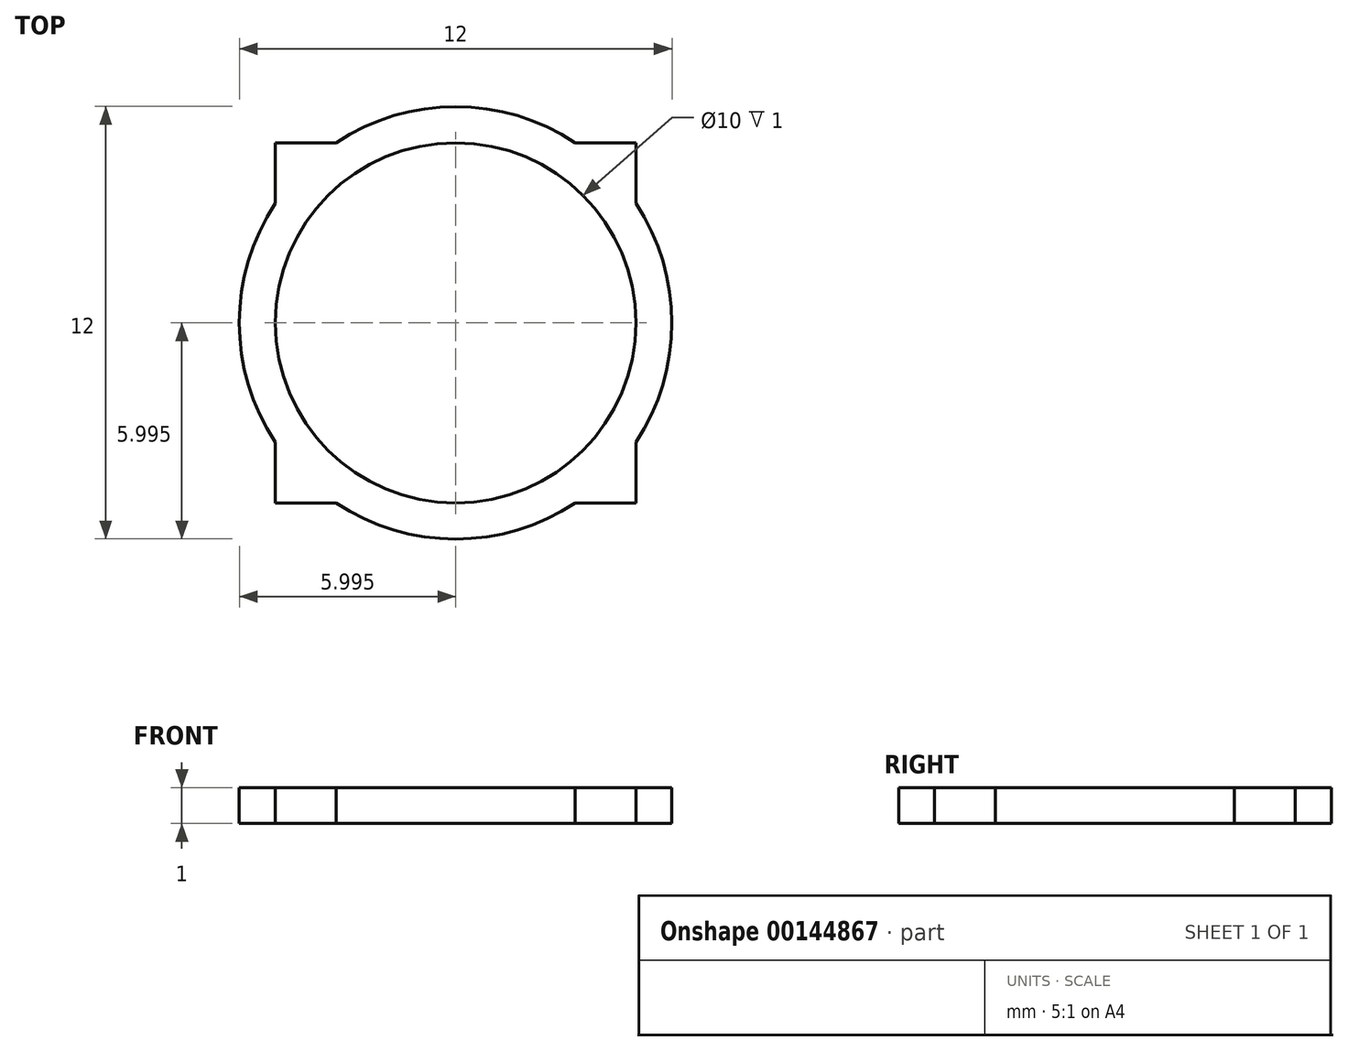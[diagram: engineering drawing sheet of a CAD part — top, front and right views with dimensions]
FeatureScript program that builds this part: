
annotation { "Feature Type Name" : "Feature", "Feature Type Description" : "" }
export const myFeature = defineFeature(function(context is Context, id is Id, definition is map)
    precondition{}
    {
        {
            var Q0;
            Q0=qCreatedBy(makeId("Top.planeOp"),FACE);
            var sketch = newSketch(context, id + "F0", { "sketchPlane" : qUnion([Q0])});
            skLineSegment(sketch, "E0", {"start": v(-26.86, -9.5) * mm, "end": v(-26.86, -19.5) * mm});
            skLineSegment(sketch, "E1", {"start": v(-26.86, -19.5) * mm, "end": v(-16.86, -19.5) * mm});
            skLineSegment(sketch, "E2", {"start": v(-16.86, -19.5) * mm, "end": v(-16.86, -9.5) * mm});
            skLineSegment(sketch, "E3", {"start": v(-26.86, -9.5) * mm, "end": v(-16.86, -9.5) * mm});
            skCircle(sketch, "E4", {"center": v(-21.86, -14.5) * mm, "radius": 5 * mm});
            skCircle(sketch, "E5", {"center": v(-21.86, -14.5) * mm, "radius": 6 * mm});
            skSolve(sketch);
        }
        {
            var Q0;
            Q0 = qSketchRegion(id + "F0", true);
            extrude(context, id + "F1", {"entities" : qUnion([Q0]), "depth" : 1 * mm});
        }
    });
